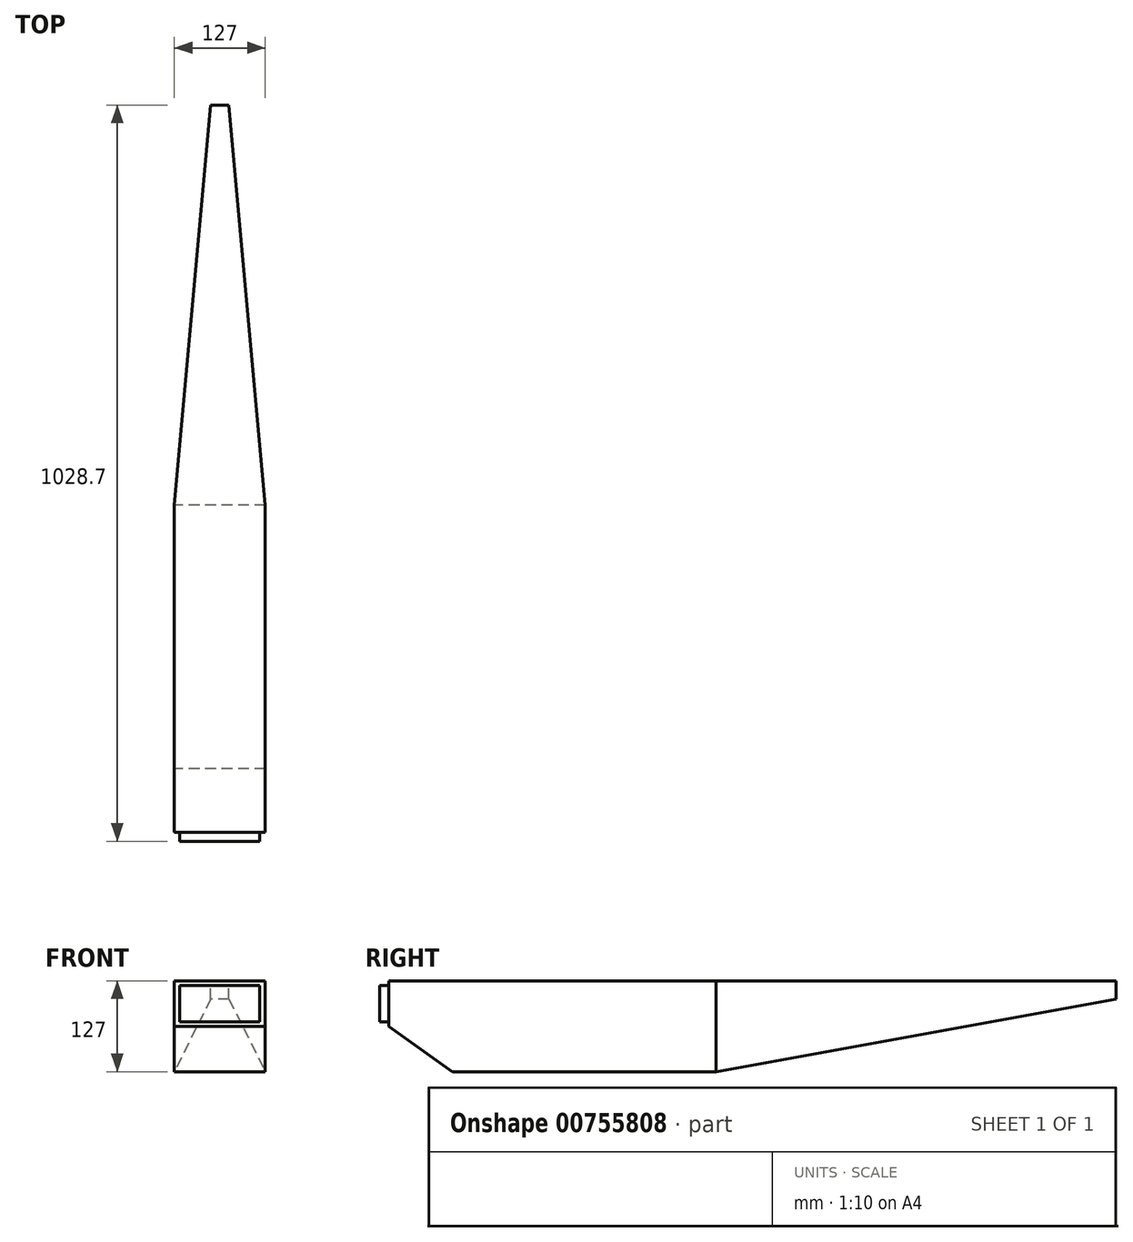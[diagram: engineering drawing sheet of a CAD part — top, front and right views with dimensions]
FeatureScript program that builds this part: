
annotation { "Feature Type Name" : "Feature", "Feature Type Description" : "" }
export const myFeature = defineFeature(function(context is Context, id is Id, definition is map)
    precondition{}
    {
        {
            var Q0;
            Q0=qCreatedBy(makeId("Right.planeOp"),FACE);
            var sketch = newSketch(context, id + "F0", { "sketchPlane" : qUnion([Q0])});
            skLineSegment(sketch, "E0.bottom", {"start": v(-949.91, 104.8) * mm, "end": v(66.09, 104.8) * mm});
            skLineSegment(sketch, "E0.top", {"start": v(-861.01, -22.2) * mm, "end": v(-492.71, -22.2) * mm});
            skLineSegment(sketch, "E0.left", {"start": v(-949.91, 104.8) * mm, "end": v(-949.91, 41.3) * mm});
            skLineSegment(sketch, "E0.right", {"start": v(66.09, 104.8) * mm, "end": v(66.09, 79.4) * mm});
            skPoint(sketch, "E1", {"position": v(66.09, 79.4) * mm});
            skPoint(sketch, "E2", {"position": v(-492.71, -22.2) * mm});
            skLineSegment(sketch, "E3", {"start": v(-492.71, -22.2) * mm, "end": v(66.09, 79.4) * mm});
            skPoint(sketch, "E4.orphan", {"position": v(66.09, -22.2) * mm});
            skPoint(sketch, "E5", {"position": v(-861.01, -22.2) * mm});
            skLineSegment(sketch, "E6", {"start": v(-949.91, 41.3) * mm, "end": v(-861.01, -22.2) * mm});
            skPoint(sketch, "E7.orphan", {"position": v(-949.91, -22.2) * mm});
            skSolve(sketch);
        }
        {
            var Q0;
            Q0=qSketchRegion(id+"F0",true);
            extrude(context, id + "F1", {"entities" : qUnion([Q0]), "depth" : 127 * mm, "offsetDistance" : 25.4 * mm});
        }
        {
            var Q0;
            Q0=makeQuery(id+"F1.opExtrude","SWEPT_FACE",FACE,{"disambiguationData":[OSD([sQuery(id+"F0.wireOp",EDGE,"E0.left")])]});
            var sketch = newSketch(context, id + "F2", { "sketchPlane" : qUnion([Q0])});
            skLineSegment(sketch, "E8.bottom", {"start": v(7.4, 98.44) * mm, "end": v(119.16, 98.44) * mm});
            skLineSegment(sketch, "E8.top", {"start": v(7.4, 47.64) * mm, "end": v(119.16, 47.64) * mm});
            skLineSegment(sketch, "E8.left", {"start": v(7.4, 98.44) * mm, "end": v(7.4, 47.64) * mm});
            skLineSegment(sketch, "E8.right", {"start": v(119.16, 98.44) * mm, "end": v(119.16, 47.64) * mm});
            skSolve(sketch);
        }
        {
            var Q0;
            Q0=qSketchRegion(id+"F2",true);
            extrude(context, id + "F3", {"entities" : qUnion([Q0]), "operationType" : NewBodyOperationType.ADD, "depth" : 12.7 * mm, "offsetDistance" : 25.4 * mm});
        }
        {
            var Q0;
            Q0=makeQuery(id+"F1.opExtrude","SWEPT_FACE",FACE,{"disambiguationData":[OSD([sQuery(id+"F0.wireOp",EDGE,"E0.bottom")])]});
            var sketch = newSketch(context, id + "F4", { "sketchPlane" : qUnion([Q0])});
            skPoint(sketch, "E9", {"position": v(127, -492.71) * mm});
            skPoint(sketch, "E10", {"position": v(63.5, 66.09) * mm});
            skPoint(sketch, "E11", {"position": v(76.2, 66.09) * mm});
            skPoint(sketch, "E12", {"position": v(50.8, 66.09) * mm});
            skPoint(sketch, "E13", {"position": v(0, -492.71) * mm});
            skLineSegment(sketch, "E14", {"start": v(50.8, 66.09) * mm, "end": v(0, -492.71) * mm});
            skLineSegment(sketch, "E15", {"start": v(76.2, 66.09) * mm, "end": v(127, -492.71) * mm});
            skLineSegment(sketch, "E16", {"start": v(127, 66.09) * mm, "end": v(76.2, 66.09) * mm});
            skLineSegment(sketch, "E17", {"start": v(0, 66.09) * mm, "end": v(0, -492.71) * mm});
            skLineSegment(sketch, "E18.trimOffspring", {"start": v(50.8, 66.09) * mm, "end": v(0, 66.09) * mm});
            skSolve(sketch);
        }
        {
            var Q0;
            Q0=makeQuery(id+"F4.imprint","IMPRINT",FACE,{"disambiguationData":[TD([[makeQuery(id+"F4.imprint","IMPRINT",EDGE,{"derivedFrom":sQuery(id+"F4.wireOp",EDGE,"E14")}),-1.0]])]});
            var Q1;
            {var subQ0=sQuery(id+"F4.wireOp",EDGE,"E15");Q1=makeQuery(id+"F4.imprint","IMPRINT",FACE,{"disambiguationData":[TD([[makeQuery(id+"F4.imprint","IMPRINT",EDGE,{"derivedFrom":subQ0}),1.0]])]});}
            extrude(context, id + "F5", {"entities" : qUnion([Q0, Q1]), "operationType" : NewBodyOperationType.REMOVE, "oppositeDirection" : true, "depth" : 138.68 * mm, "offsetDistance" : 25.4 * mm});
        }
    });
